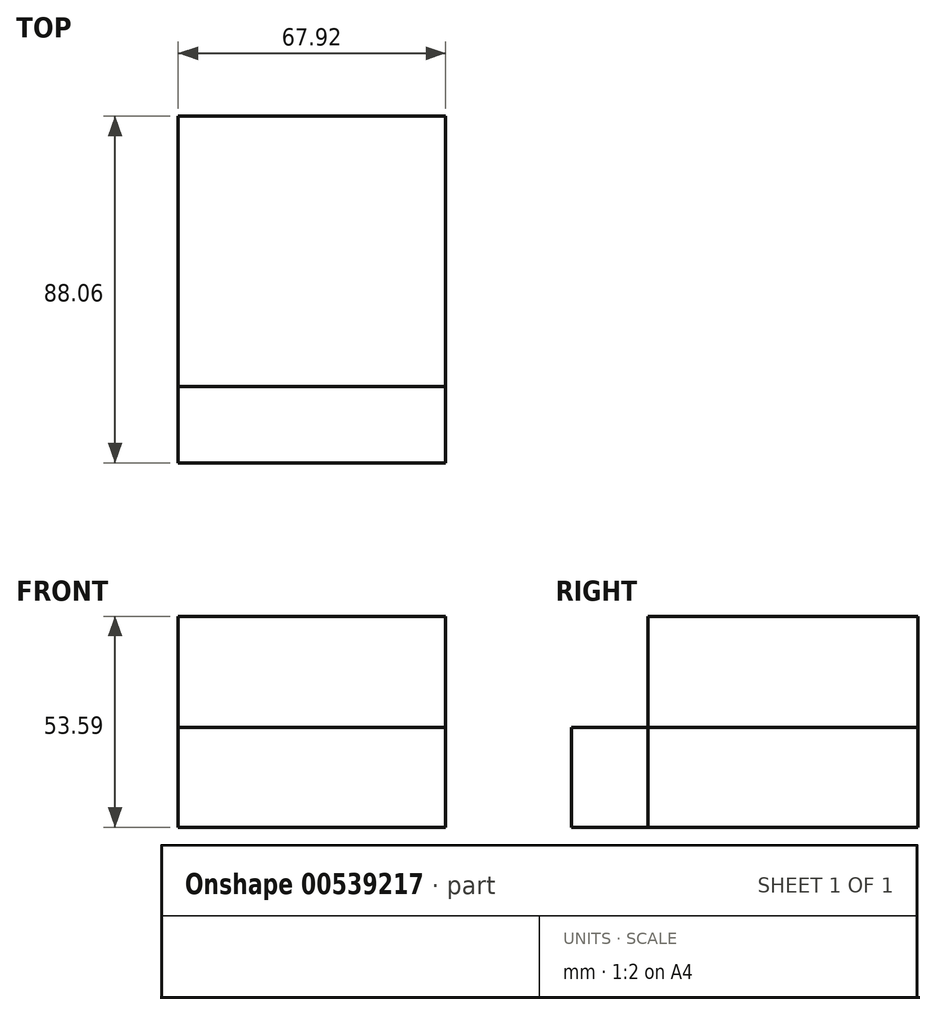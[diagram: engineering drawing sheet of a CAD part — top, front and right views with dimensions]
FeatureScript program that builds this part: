
annotation { "Feature Type Name" : "Feature", "Feature Type Description" : "" }
export const myFeature = defineFeature(function(context is Context, id is Id, definition is map)
    precondition{}
    {
        {
            var Q0;
            Q0=qCreatedBy(makeId("Top.planeOp"),FACE);
            var sketch = newSketch(context, id + "F0", { "sketchPlane" : qUnion([Q0])});
            skLineSegment(sketch, "E0.bottom", {"start": v(33.96, 44.03) * mm, "end": v(-33.96, 44.03) * mm});
            skLineSegment(sketch, "E0.top", {"start": v(33.96, -44.03) * mm, "end": v(-33.96, -44.03) * mm});
            skLineSegment(sketch, "E0.left", {"start": v(33.96, 44.03) * mm, "end": v(33.96, -44.03) * mm});
            skLineSegment(sketch, "E0.right", {"start": v(-33.96, 44.03) * mm, "end": v(-33.96, -44.03) * mm});
            skPoint(sketch, "E0.middle", {"position": v(0, 0) * mm});
            skSolve(sketch);
        }
        {
            var Q0;
            Q0=makeQuery(id+"F0.imprint","IMPRINT",FACE,{"disambiguationData":[TD([[makeQuery(id+"F0.imprint","IMPRINT",EDGE,{"derivedFrom":sQuery(id+"F0.wireOp",EDGE,"E0.bottom")}),1.0]])]});
            extrude(context, id + "F1", {"entities" : qUnion([Q0]), "depth" : 53.6 * mm, "offsetDistance" : 25.4 * mm});
        }
        {
            var Q0;
            Q0=makeQuery(id+"F1.opExtrude","CAP_FACE",FACE,{"disambiguationData":[OSD([sQuery(id+"F0.wireOp",EDGE,"E0.bottom"),sQuery(id+"F0.wireOp",EDGE,"E0.top"),sQuery(id+"F0.wireOp",EDGE,"E0.left"),sQuery(id+"F0.wireOp",EDGE,"E0.right")])],"isStart":false});
            var sketch = newSketch(context, id + "F2", { "sketchPlane" : qUnion([Q0])});
            skLineSegment(sketch, "E1.bottom", {"start": v(-33.96, -44.03) * mm, "end": v(33.96, -44.03) * mm});
            skLineSegment(sketch, "E1.top", {"start": v(-33.96, -24.6) * mm, "end": v(33.96, -24.6) * mm});
            skLineSegment(sketch, "E1.left", {"start": v(-33.96, -44.03) * mm, "end": v(-33.96, -24.6) * mm});
            skLineSegment(sketch, "E1.right", {"start": v(33.96, -44.03) * mm, "end": v(33.96, -24.6) * mm});
            skSolve(sketch);
        }
        {
            var Q0;
            Q0=makeQuery(id+"F2.imprint","IMPRINT",FACE,{"disambiguationData":[TD([[makeQuery(id+"F2.imprint","IMPRINT",EDGE,{"derivedFrom":sQuery(id+"F2.wireOp",EDGE,"E1.bottom")}),-1.0]])]});
            extrude(context, id + "F3", {"entities" : qUnion([Q0]), "operationType" : NewBodyOperationType.REMOVE, "oppositeDirection" : true, "depth" : 89.66 * mm, "offsetDistance" : 25.4 * mm});
        }
        {
            var Q0;
            Q0=makeQuery(id+"F0.imprint","IMPRINT",FACE,{"disambiguationData":[TD([[makeQuery(id+"F0.imprint","IMPRINT",EDGE,{"derivedFrom":sQuery(id+"F0.wireOp",EDGE,"E0.bottom")}),1.0]])]});
            extrude(context, id + "F4", {"entities" : qUnion([Q0]), "depth" : 25.4 * mm});
        }
    });
